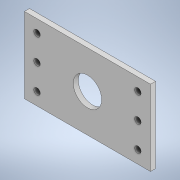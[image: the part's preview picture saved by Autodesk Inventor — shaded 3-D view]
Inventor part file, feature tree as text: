
AUTODESK INVENTOR PART (.ipt)
format: ipt  version: 2020 (Build 240168000, 168)  size: 118,272 bytes
history: native  units: in
note: dims shown in document units (in); Inventor stores cm internally (conversion verified against a paired STEP export)
features: extrude x1, sketch x1
ambient origin geometry x8: Origin, YZ Plane, XZ Plane, XY Plane, X Axis, Y Axis, Z Axis, Center Point
bodies: Body1 (feature_tree)
feature tree (2):
  extrude  "Extrusion2"  Depth=3.0in
  sketch  "Sketch1"  dims[d0=5.0in d1=3.0in d2=1.5in d3=2.5in d4=1.125in d5=0.256in d6=0.5in d7=0.5in d8=1.1811in d10=1.0in d11=0.3937in d13=1.0in d17=0.7874in d19=4.0in d20=0.3937in d22=1.0in d24=0.2in d25=0.0in]
